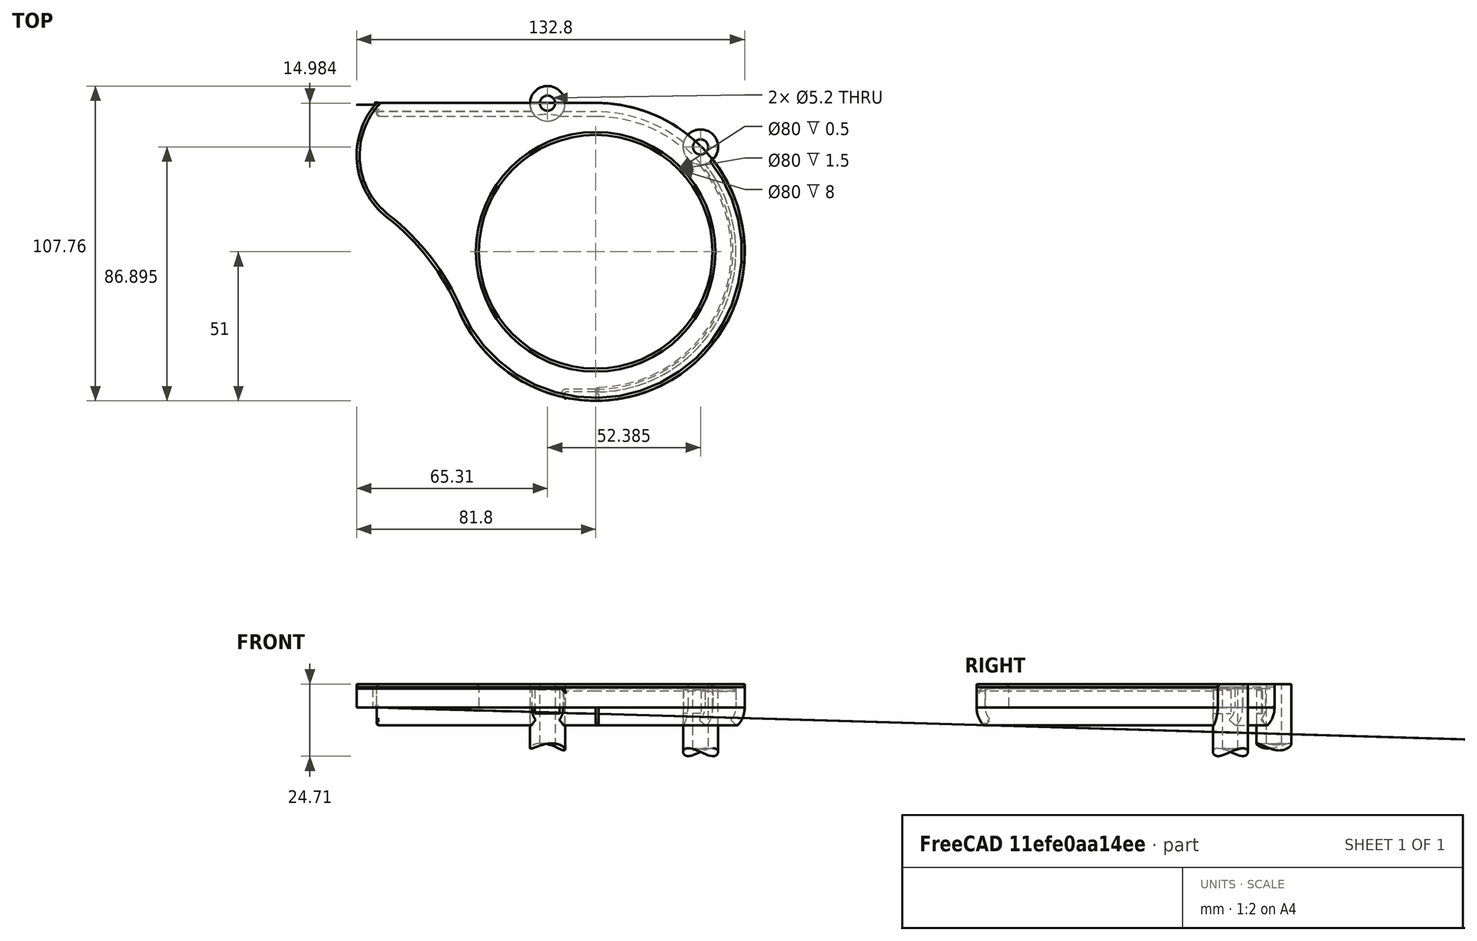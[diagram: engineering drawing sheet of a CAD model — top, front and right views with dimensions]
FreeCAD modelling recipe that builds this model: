
FCSTD DOCUMENT  (FreeCAD 0.16R)
Label: SimpleChainguard4
License: All rights reserved
LicenseURL: http://en.wikipedia.org/wiki/All_rights_reserved
objects: Sketcher::SketchObject×6, Part::Cylinder×4, PartDesign::Pad×3, Part::Cut×3, PartDesign::Chamfer×3, PartDesign::Pocket×2, Part::MultiFuse×2, PartDesign::Fillet×2, PartDesign::Revolution×1, Mesh::Feature×1
note: 32 computed .brp shape members not serialized (recipe doc carries the construction recipe); baked Part::Feature solids carry a one-line shape summary decoded from their .brp

FEATURE [Sketcher::SketchObject] Sketch
  sketch-geometry (7):
    g0: Circle CenterX=0 CenterY=0 CenterZ=0 NormalX=0 NormalY=0 NormalZ=1 Radius=40
    g1: ArcOfCircle CenterX=0 CenterY=0 CenterZ=0 NormalX=0 NormalY=0 NormalZ=1 Radius=51 StartAngle=3.54457 EndAngle=7.85398
    g2: LineSegment StartX=-75 StartY=51 StartZ=0 EndX=0 EndY=51 EndZ=0
    g3: ArcOfCircle CenterX=-54.8043 CenterY=33.0798 CenterZ=0 NormalX=0 NormalY=0 NormalZ=1 Radius=27 StartAngle=2.41582 EndAngle=4.05122
    g4: ArcOfCircle CenterX=-120.507 CenterY=-51.3726 CenterZ=0 NormalX=0 NormalY=0 NormalZ=1 Radius=80 StartAngle=0.402976 EndAngle=0.909627
    g5: LineSegment [constr] StartX=0 StartY=0 StartZ=0 EndX=114.907 EndY=96.4181 EndZ=0
    g6: LineSegment [constr] StartX=-46.3525 StartY=142.658 StartZ=0 EndX=0 EndY=0 EndZ=0
  constraints (22):
    c: Radius(g0) = 40
    c: Coincident(g0,g-1)
    c: Coincident(g1,g-1)
    c: PointOnObject(g1,g-2)
    c: Coincident(g2,g1)
    c: Horizontal(g2)
    c: Distance(g2) = 75
    c: Coincident(g3,g2)
    c: Coincident(g4,g3)
    c: Coincident(g4,g1)
    c: Tangent(g4,g3)
    c: Tangent(g1,g4)
    c: Radius(g1) = 51
    c: Radius(g4) = 80
    c: Radius(g3) = 27
    c: Coincident(g5,g-1)
    c: Angle(g6) = -1.25664
    c: Coincident(g6,g-1)
    c: Angle(g5) = 0.698132
    c: Distance(g5) = 150
    c: Distance(g6) = 150
    c: DistanceY(g1) = -20
FEATURE [PartDesign::Pad] Pad
  Length = 8
  Length2 = 100
  Sketch = -> Sketch
  Type = 0
FEATURE [Sketcher::SketchObject] Sketch001
  ExternalGeometry = -> [Pad]
  Placement = pos=(0,0,0) rot=(1,0,0;3.14159rad)
  Support = -> Pad [Face6]
  sketch-geometry (4):
    g0: LineSegment StartX=-146.216 StartY=-48 StartZ=0 EndX=0 EndY=-48 EndZ=0
    g1: ArcOfCircle CenterX=0 CenterY=0 CenterZ=0 NormalX=0 NormalY=0 NormalZ=1 Radius=48 StartAngle=4.71239 EndAngle=7.85398
    g2: LineSegment StartX=0 StartY=48 StartZ=0 EndX=-146.216 EndY=48 EndZ=0
    g3: LineSegment StartX=-146.216 StartY=-48 StartZ=0 EndX=-146.216 EndY=48 EndZ=0
  constraints (12):
    c: Coincident(g1,g-1)
    c: PointOnObject(g1,g-2)
    c: Coincident(g2,g1)
    c: Horizontal(g2)
    c: Coincident(g3,g0)
    c: Coincident(g3,g2)
    c: Vertical(g3)
    c: Distance(g2) = 146.216
    c: Coincident(g0,g1)
    c: PointOnObject(g0,g-2)
    c: Distance(g-4,g0) = 3
    c: Horizontal(g0)
FEATURE [PartDesign::Pocket] Pocket
  Length = 6.5
  Sketch = -> Sketch001
  Type = 0
FEATURE [Sketcher::SketchObject] Sketch004
  Placement = pos=(0,0,0) rot=(0.57735,0.57735,0.57735;2.0944rad)
  sketch-geometry (6):
    g0: LineSegment StartX=48.3639 StartY=-6.36399 StartZ=0 EndX=46.2426 EndY=-4.24266 EndZ=0
    g1: ArcOfCircle CenterX=42 CenterY=0 CenterZ=0 NormalX=0 NormalY=0 NormalZ=1 Radius=6 StartAngle=5.49778 EndAngle=6.28319
    g2: ArcOfCircle CenterX=42 CenterY=0 CenterZ=0 NormalX=0 NormalY=0 NormalZ=1 Radius=9 StartAngle=5.49778 EndAngle=6.28319
    g3: LineSegment [constr] StartX=35.4204 StartY=-19.3075 StartZ=0 EndX=48.3639 EndY=-6.36399 EndZ=0
    g4: LineSegment [constr] StartX=20.3373 StartY=-30.148 StartZ=0 EndX=46.2426 EndY=-4.24266 EndZ=0
    g5: LineSegment StartX=48 StartY=0 StartZ=0 EndX=51 EndY=0 EndZ=0
  constraints (19):
    c: Coincident(g2,g1)
    c: Parallel(g3,g4)
    c: Angle(g4) = 0.785398
    c: Coincident(g0,g2)
    c: Coincident(g0,g1)
    c: Coincident(g5,g1)
    c: Coincident(g5,g2)
    c: Perpendicular(g2,g0)
    c: DistanceX(g1) = 42
    c: Distance(g3) = 18.3049
    c: Distance(g4) = 36.6357
    c: Distance(g5) = 3
    c: Coincident(g0,g3)
    c: Coincident(g4,g0)
    c: Tangent(g4,g1)
    c: Horizontal(g5)
    c: Perpendicular(g2,g5)
    c: DistanceX(g2) = 51
    c: PointOnObject(g2,g-1)
FEATURE [PartDesign::Revolution] Revolution
  Angle = 180
  Axis = (0,0,1)
  Base = (0,0,0)
  Placement = pos=(0,0,0) rot=(0.57735,0.57735,0.57735;2.0944rad)
  ReferenceAxis = -> Sketch004 [V_Axis]
  Reversed = true
  Sketch = -> Sketch004
FEATURE [Sketcher::SketchObject] Sketch005
  sketch-geometry (4):
    g0: LineSegment [constr] StartX=-45.1089 StartY=138.831 StartZ=0 EndX=0 EndY=0 EndZ=0
    g1: LineSegment [constr] StartX=122.75 StartY=122.75 StartZ=0 EndX=0 EndY=0 EndZ=0
    g2: Circle CenterX=-16.4924 CenterY=50.7583 CenterZ=0 NormalX=0 NormalY=0 NormalZ=1 Radius=6
    g3: Circle CenterX=35.8947 CenterY=35.8947 CenterZ=0 NormalX=0 NormalY=0 NormalZ=1 Radius=6
  constraints (8):
    c: Coincident(g0,g-1)
    c: Coincident(g1,g-1)
    c: Angle(g1) = -2.35619
    c: Angle(g0) = -1.25664
    c: Radius(g2) = 6
    c: PointOnObject(g2,g0)
    c: Radius(g3) = 6
    c: PointOnObject(g3,g1)
FEATURE [PartDesign::Pad] Pad001
  Length = 8
  Length2 = 25
  Sketch = -> Sketch005
  Type = 4
FEATURE [Sketcher::SketchObject] Sketch006
  Placement = pos=(0,0,0) rot=(0.57735,0.57735,0.57735;2.0944rad)
  sketch-geometry (6):
    g0: LineSegment StartX=48.3639 StartY=-6.36399 StartZ=0 EndX=46.2426 EndY=-4.24266 EndZ=0
    g1: ArcOfCircle CenterX=42 CenterY=0 CenterZ=0 NormalX=0 NormalY=0 NormalZ=1 Radius=6 StartAngle=5.49778 EndAngle=6.28319
    g2: ArcOfCircle CenterX=42 CenterY=0 CenterZ=0 NormalX=0 NormalY=0 NormalZ=1 Radius=9 StartAngle=5.49778 EndAngle=6.28319
    g3: LineSegment [constr] StartX=35.4204 StartY=-19.3075 StartZ=0 EndX=48.3639 EndY=-6.36399 EndZ=0
    g4: LineSegment [constr] StartX=20.3373 StartY=-30.148 StartZ=0 EndX=46.2426 EndY=-4.24266 EndZ=0
    g5: LineSegment StartX=48 StartY=0 StartZ=0 EndX=51 EndY=0 EndZ=0
  constraints (19):
    c: Coincident(g2,g1)
    c: Parallel(g3,g4)
    c: Angle(g4) = 0.785398
    c: Coincident(g0,g2)
    c: Coincident(g0,g1)
    c: Coincident(g5,g1)
    c: Coincident(g5,g2)
    c: Perpendicular(g2,g0)
    c: DistanceX(g1) = 42
    c: Distance(g3) = 18.3049
    c: Distance(g4) = 36.6357
    c: Distance(g5) = 3
    c: Coincident(g0,g3)
    c: Coincident(g4,g0)
    c: Tangent(g4,g1)
    c: Horizontal(g5)
    c: Perpendicular(g2,g5)
    c: DistanceX(g2) = 51
    c: PointOnObject(g2,g-1)
FEATURE [PartDesign::Pad] Pad002
  Length = 75
  Length2 = 100
  Placement = pos=(0,0,0) rot=(0.57735,0.57735,0.57735;2.0944rad)
  Reversed = true
  Sketch = -> Sketch006
  Type = 0
FEATURE [Part::Cylinder] Cylinder
  Angle = 360
  Height = 100
  Placement = pos=(0,0,-22) rot=(0.948683,0.316228,0;4.71239rad)
  Radius = 9.7
FEATURE [Part::Cylinder] Cylinder001
  Angle = 360
  Height = 100
  Placement = pos=(0,0,-22) rot=(-0.707107,0.707107,0;1.5708rad)
  Radius = 8
FEATURE [Part::MultiFuse] Fusion
  Shapes = -> [Pocket,Revolution,Pad001,Pad002]
FEATURE [Part::MultiFuse] Fusion001
  Shapes = -> [Cylinder001,Cylinder]
FEATURE [Part::Cut] Cut
  Base = -> Fusion
  Tool = -> Fusion001
FEATURE [PartDesign::Fillet] Fillet
  Base = -> Cut [Edge27,Edge17,Edge91,Edge87,Edge75,Edge77]
  Radius = 1
FEATURE [PartDesign::Fillet] Fillet001
  Base = -> Fillet [Edge79,Edge77,Edge93,Edge91,Edge105,Edge97,Edge110,Edge107]
  Radius = 0.5
FEATURE [Sketcher::SketchObject] Sketch007
  ExternalGeometry = -> [Fillet001]
  Placement = pos=(0,0,8) rot=(0,0,1;0rad)
  Support = -> Fillet001 [Face48]
  sketch-geometry (2):
    g0: Circle CenterX=35.8947 CenterY=35.8947 CenterZ=0 NormalX=0 NormalY=0 NormalZ=1 Radius=2.6
    g1: Circle CenterX=-16.4899 CenterY=50.8791 CenterZ=0 NormalX=0 NormalY=0 NormalZ=1 Radius=2.6
  constraints (4):
    c: Radius(g1) = 2.6
    c: Equal(g1,g0)
    c: Symmetric(g-4,g-4,g1)
    c: Coincident(g0,g-6)
FEATURE [PartDesign::Pocket] Pocket001
  Length = 5
  Sketch = -> Sketch007
  Type = 1
FEATURE [Part::Cylinder] Cylinder002
  Angle = 360
  Height = 8
  Placement = pos=(-17,27,-2) rot=(0,0,1;0rad)
  Radius = 20
FEATURE [Part::Cylinder] Cylinder003
  Angle = 360
  Height = 8
  Placement = pos=(12,12,-2) rot=(0,0,1;0rad)
  Radius = 30
FEATURE [Part::Cut] Cut001
  Base = -> Pocket001
  Tool = -> Cylinder003
FEATURE [Part::Cut] Cut002
  Base = -> Cut001
  Tool = -> Cylinder002
FEATURE [PartDesign::Chamfer] Chamfer
  Base = -> Cut002 [Edge127]
  Size = 1
FEATURE [PartDesign::Chamfer] Chamfer001
  Base = -> Chamfer [Edge28]
  Size = 1
FEATURE [PartDesign::Chamfer] Chamfer002
  Base = -> Chamfer001 [Edge120]
  Size = 1
FEATURE [Mesh::Feature] Mesh  label="Chamfer002 (Meshed)"
